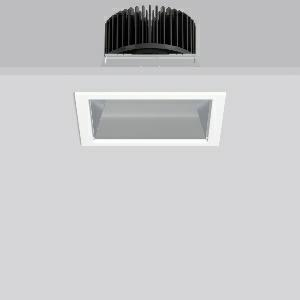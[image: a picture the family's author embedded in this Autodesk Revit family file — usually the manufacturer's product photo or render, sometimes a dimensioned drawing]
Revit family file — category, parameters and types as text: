
# Revit family: quardo_901706_002_1_76_4852
name_source: partatom
category: Lighting Fixtures
units: mm (PartAtom-declared; Revit-internal decimal feet)

## family parameters
Cut with Voids When Loaded = No
Host = Face
Light Source = No
Part Type = Normal
Room Calculation Point = No
Round Connector Dimension = Use Diameter
Shared = No

## types (1)
- QUARDO (1 x LED Modul 840, 4450 lm, 4000)
    Apparent Load = 37 VA
    CIE Flux Codes = 81 100 100 100 100
    Color Rendering = 80
    Color Temperature = 4000
    Default Elevation = 1800 mm
    Description = Series: QUARDO
High-quality recessed downlight with square luminous surface. Recessed mounting frame: die-cast aluminium, powder-coated. Mounting bracket: galvanised sheet steel. Reflector: aluminium, highly polished anodised finish. Ceiling installation with spring system. Including separate LED converter with connecting cable 600 mm. Through-wiring box (5 pole) available as accessory. 
Colour: traffic white, matt (RAL 9016)
Length: 176 mm
Width: 176 mm
Height: 4 mm
Cut-out length: 165 mm
Cut-out width: 165 mm
Recess height: 150 mm
Luminaire: recess height: 145 mm
Lamp: LED
Socket: without socket
Colour temperature: 4000K
Colour rendering index (CRI): 85
System power: 37 W
Rated luminous flux: 4450 lm
Luminous efficiency: 120 lm/W
Control gear: Converter, dimmable, DALI
Protection class: II
Type of protection: IP 20
    Height = 0 mm  [stored 0 ft]
    Lamp = 1 x LED Modul 840
    Lamp Light Flux = 4450 lm
    Lamp count = 1
    Length = 176 mm
    Lifetime = 50000 h
    Luminous efficacy = 120 lm/W
    Manufacturer = RZB
    ModVariant = No
    Model = 901706.002.1.76
    Mounting Place = Ceiling
    Mounting Type = Recessed
    Number of Poles = 1
    OnlyDefault = Yes
    Power Factor = 1
    Product Name = QUARDO
    Product group = Recessed downlights
    ProductGroupID = 402
    Protection Class = Protection class II
    Protection Degree = IP 20
    RLX_Detail_Level = 1
    RLX_Emergency_Light_Flux = 0 lm
    RLX_Emergency_Type = 0
    RLX_Emergency_Type_DB = No
    RlxData = <blob elided: 29273 chars, md5=534e44ee>
    Socket = socket
    Standby Power = 0 W
    System Light Flux = 4450 lm
    System Power = 37 W
    Type Comments = Product without accessories
    Type Image = 901705.002.jpg
    URL = http://relux.com
    VarID = ---
    Voltage = 230 V
    Voltage Range = 220-240 V
    Weight = 0.00 kg
    Width = 176 mm

note: [stored X ft] marks values corroborated as IEEE doubles in the binary element streams (Revit-internal decimal feet)

## geometry (parser evidence)
native form markers: Blend x4, Sweep x10
no freeform markers — native parametric forms only
